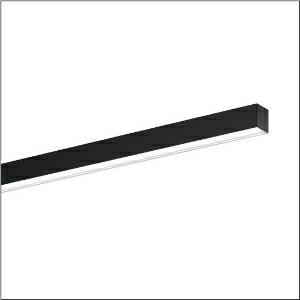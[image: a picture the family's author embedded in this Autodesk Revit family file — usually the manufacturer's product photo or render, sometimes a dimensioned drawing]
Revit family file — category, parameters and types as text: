
# Revit family: silica_21_51mx20tct5b
name_source: partatom
category: Lighting Fixtures
units: mm (PartAtom-declared; Revit-internal decimal feet)

## family parameters
Cut with Voids When Loaded = No
Host = Face
Light Source = No
Part Type = Normal
Room Calculation Point = No
Round Connector Dimension = Use Diameter
Shared = No

## types (1)
- --- (1 x LED, 6000 lm, 51.3 W, 6500K)
    Apparent Load = 51 VA
    CIE Flux Codes = 48 79 96 100 100
    Color Rendering = 80
    Color Temperature = 6500K
    Default Elevation = 1800 mm
    Description = Silica 21, office luminaire, primary optical cover: cover, of PMMA, opal, light emission: direct distribution, primary light characteristic: symmetric, installation type: surface-mounted, LED, rated luminous flux: 6.000lm, luminous efficacy: 112lm/W, light colour: 8tw, colour temperature: 2700..6500K, control gear: DALI DT8, with terminal, 3+2-pole, max. 2.5mm², mains connection: 220..240V, AC, 50/60Hz, rated input power: 53.8W, luminaire housing, of aluminium, matt jet black (RAL 9005), length: 3.004mm, width: 53mm, height: 53mm, protection rating (complete): IP20, insulation class (complete): insulation class I (protective earthing), certification: CE, permissible operating ambient temperature: 0..+35°C, standard: EN 50419, packaging unit: 1 piece
    Height = 53 mm
    Lamp = 1 x LED
    Lamp Light Flux = 6000 lm
    Lamp Power = 51.3 W
    Lamp count = 1
    Length = 3004 mm
    Luminous efficacy = 117 lm/W
    Manufacturer = Siteco
    ModVariant = No
    Model = 51MX20TCT5B
    Mounting Place = Ceiling
    Mounting Type = Surface mounted
    Number of Poles = 1
    OnlyDefault = Yes
    Power Factor = 1
    Product Name = Silica 21
    Product group = office luminaire | ceiling mounted
    ProductGroupID = 301
    Protection Class = Protection class I
    Protection Degree = IP 20
    RLX_Detail_Level = 1
    RLX_Emergency_Light_Flux = 0 lm
    RLX_Emergency_Type = 0
    RLX_Emergency_Type_DB = No
    RlxData = <blob elided: 25617 chars, md5=31d8a69e>
    Socket = socket
    Standby Power = 0 W
    System Light Flux = 6000 lm
    System Power = 51 W
    Type Comments = individual setting
    Type Image = l_1335925.jpg
    URL = http://relux.com
    VarID = @adj_139175
    Voltage = 0 V
    Weight = 0.00 kg
    Width = 53 mm

## geometry (parser evidence)
native form markers: Blend x4, Sweep x10
no freeform markers — native parametric forms only
